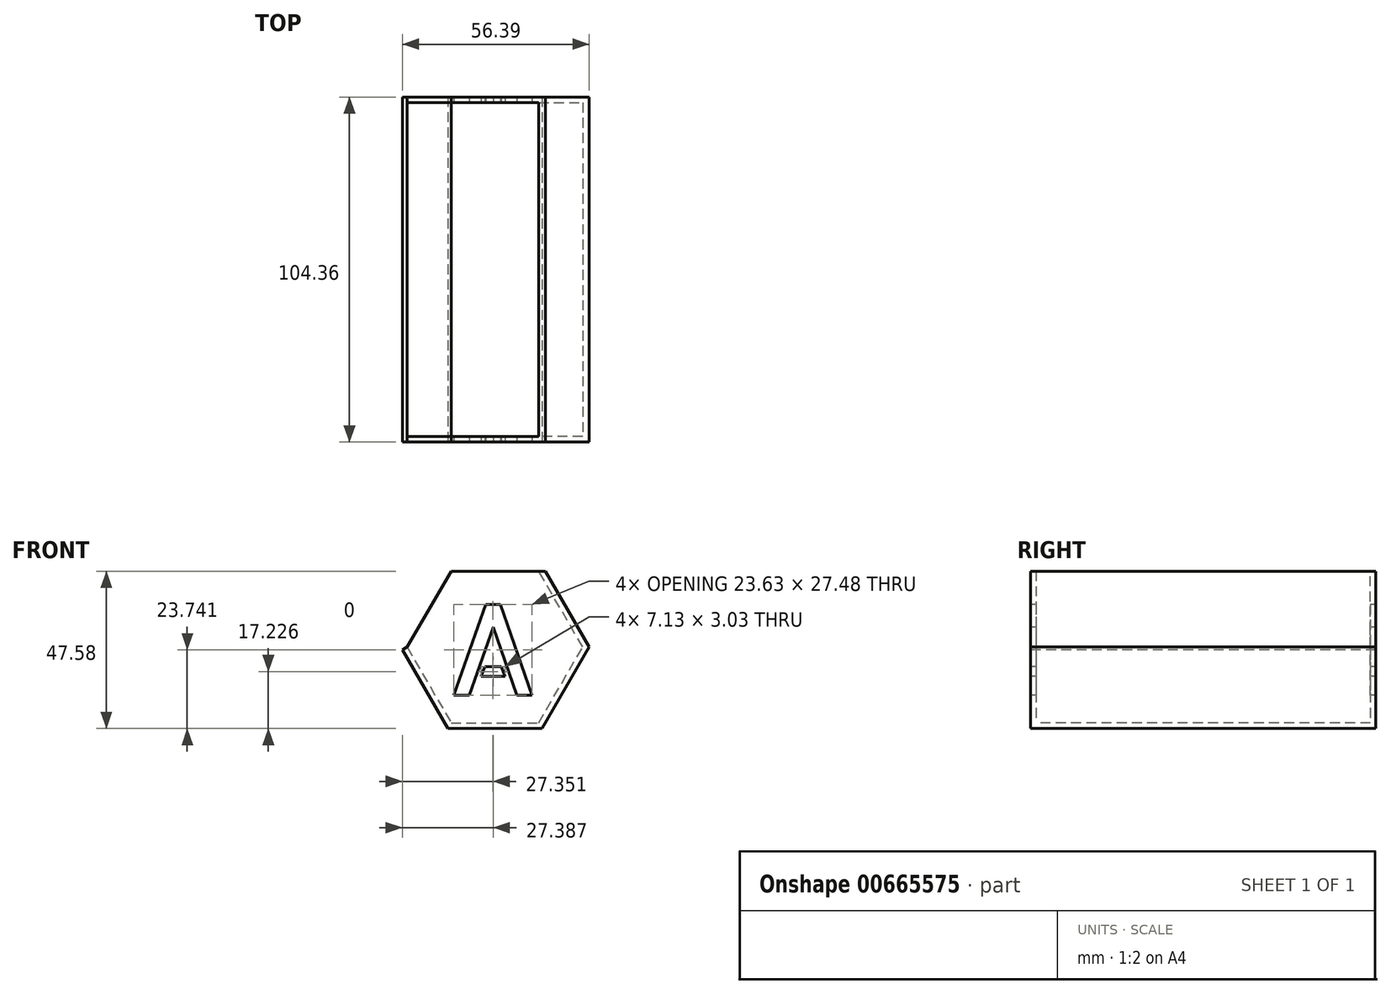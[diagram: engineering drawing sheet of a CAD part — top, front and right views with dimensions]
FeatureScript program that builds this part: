
annotation { "Feature Type Name" : "Feature", "Feature Type Description" : "" }
export const myFeature = defineFeature(function(context is Context, id is Id, definition is map)
    precondition{}
    {
        {
            assignVariable(context, id + "F0", {"name" : "printerclearance", "anyValue" : 1});
        }
        {
            assignVariable(context, id + "F1", {"name" : "wall", "anyValue" : 1.68});
        }
        {
            assignVariable(context, id + "F2", {"name" : "stacklength", "anyValue" : 100 + getVariable(context, 'printerclearance')});
        }
        {
            var Q0;
            Q0=qCreatedBy(makeId("Front.planeOp"),FACE);
            var sketch = newSketch(context, id + "F3", { "sketchPlane" : qUnion([Q0])});
            skLineSegment(sketch, "E0", {"start": v(0, 0) * mm, "end": v(26.5, 0) * mm});
            skLineSegment(sketch, "E1", {"start": v(26.5, 0) * mm, "end": v(39.75, 22.95) * mm});
            skLineSegment(sketch, "E2", {"start": v(39.75, 22.95) * mm, "end": v(26.5, 45.9) * mm});
            skLineSegment(sketch, "E3", {"start": v(26.5, 45.9) * mm, "end": v(0, 45.9) * mm});
            skLineSegment(sketch, "E4", {"start": v(0, 45.9) * mm, "end": v(-13.25, 22.95) * mm});
            skLineSegment(sketch, "E5", {"start": v(-13.25, 22.95) * mm, "end": v(0, 0) * mm});
            skSolve(sketch);
        }
        {
            var Q0;
            Q0=makeQuery(id+"F3.imprint","IMPRINT",FACE,{"disambiguationData":[TD([[makeQuery(id+"F3.imprint","IMPRINT",EDGE,{"derivedFrom":sQuery(id+"F3.wireOp",EDGE,"E0")}),1.0]])]});
            var sketch = newSketch(context, id + "F4", { "sketchPlane" : qUnion([Q0])});
            skLineSegment(sketch, "E6.0", {"start": v(41.69, 22.95) * mm, "end": v(28.44, 45.9) * mm});
            skLineSegment(sketch, "E6.1", {"start": v(27.47, -1.68) * mm, "end": v(41.69, 22.95) * mm});
            skLineSegment(sketch, "E6.2", {"start": v(-0.97, -1.68) * mm, "end": v(27.47, -1.68) * mm});
            skLineSegment(sketch, "E6.3", {"start": v(-14.7, 22.1) * mm, "end": v(-0.97, -1.68) * mm});
            skLineSegment(sketch, "E7", {"start": v(-14.7, 22.1) * mm, "end": v(-13.25, 22.95) * mm});
            skLineSegment(sketch, "E8", {"start": v(28.44, 45.9) * mm, "end": v(26.5, 45.9) * mm});
            skLineSegment(sketch, "E9", {"start": v(0, 45.9) * mm, "end": v(26.5, 45.9) * mm});
            skLineSegment(sketch, "E10", {"start": v(0, 45.9) * mm, "end": v(-13.25, 22.95) * mm});
            skSolve(sketch);
        }
        {
            var Q0;
            Q0 = qSketchRegion(id + "F4", true);
            extrude(context, id + "F5", {"entities" : qUnion([Q0]), "oppositeDirection" : true, "depth" : (getVariable(context, 'stacklength') + getVariable(context, 'wall')) * mm, "offsetDistance" : 25 * mm, "hasSecondDirection" : true, "secondDirectionOppositeDirection" : false, "secondDirectionDepth" : (getVariable(context, 'wall')) * mm});
        }
        {
            var Q0;
            Q0 = qSketchRegion(id + "F3", true);
            extrude(context, id + "F6", {"entities" : qUnion([Q0]), "operationType" : NewBodyOperationType.REMOVE, "oppositeDirection" : true, "depth" : (getVariable(context, 'stacklength')) * mm, "offsetDistance" : 25 * mm});
        }
        {
            var Q0;
            Q0=makeQuery(id+"F5.opExtrude","CAP_FACE",FACE,{"disambiguationData":[OSD([sQuery(id+"F4.wireOp",EDGE,"E6.0"),sQuery(id+"F4.wireOp",EDGE,"E6.1"),sQuery(id+"F4.wireOp",EDGE,"E6.2"),sQuery(id+"F4.wireOp",EDGE,"E6.3"),sQuery(id+"F4.wireOp",EDGE,"E7"),sQuery(id+"F4.wireOp",EDGE,"E8"),sQuery(id+"F4.wireOp",EDGE,"E9"),sQuery(id+"F4.wireOp",EDGE,"E10")])],"isStart":true});
            var sketch = newSketch(context, id + "F7", { "sketchPlane" : qUnion([Q0])});
            skText(sketch, "E11", { "text": "A", "fontName": "AllertaStencil-Regular.ttf"});
            skLineSegment(sketch, "E12", {"start": v(13.25, -1.68) * mm, "end": v(13.25, 8.32) * mm, "construction": true});
            skLineSegment(sketch, "E13", {"start": v(41.69, 22.95) * mm, "end": v(28.42, 22.95) * mm, "construction": true});
            const initialGuessF7  = {"E11": [-0.00152, 0.00832, 1, 0, 0.02753]};
            skSetInitialGuess(sketch, initialGuessF7);
            skSolve(sketch);
        }
        {
            var Q0;
            Q0 = qSketchRegion(id + "F7", true);
            extrude(context, id + "F8", {"entities" : qUnion([Q0]), "operationType" : NewBodyOperationType.REMOVE, "oppositeDirection" : true, "depth" : (getVariable(context, 'stacklength') * 2) * mm, "offsetDistance" : 25 * mm});
        }
    });
